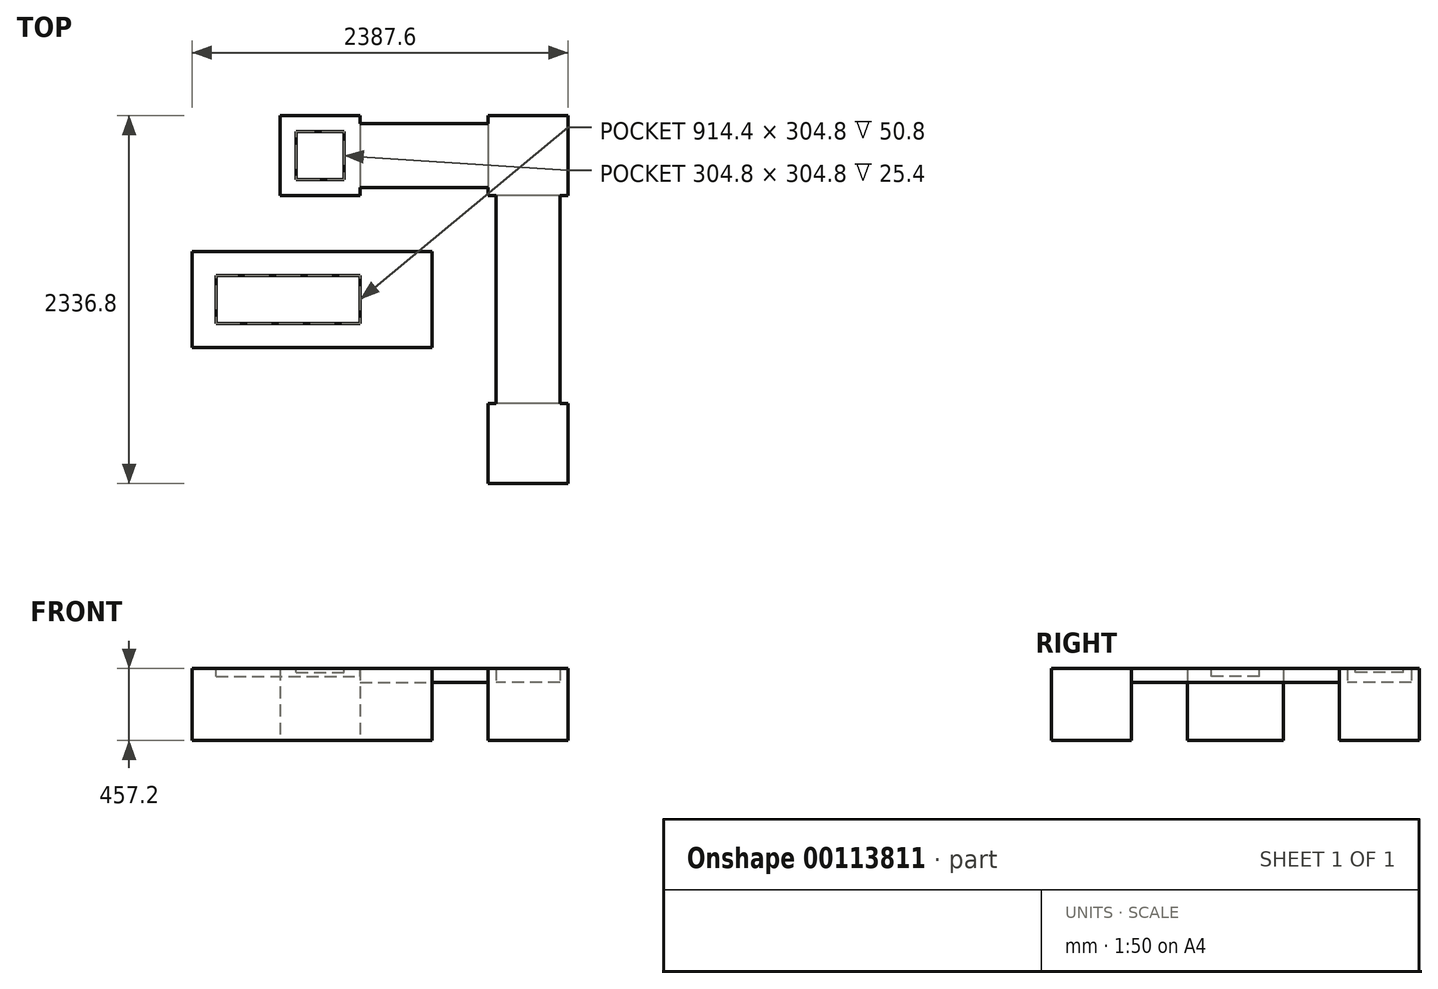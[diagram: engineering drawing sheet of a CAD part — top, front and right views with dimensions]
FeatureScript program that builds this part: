
annotation { "Feature Type Name" : "Feature", "Feature Type Description" : "" }
export const myFeature = defineFeature(function(context is Context, id is Id, definition is map)
    precondition{}
    {
        {
            var Q0;
            Q0=qCreatedBy(makeId("Top.planeOp"),FACE);
            var sketch = newSketch(context, id + "F0", { "sketchPlane" : qUnion([Q0])});
            skLineSegment(sketch, "E0.bottom", {"start": v(-2438.4, 2336.8) * mm, "end": v(0, 2336.8) * mm, "construction": true});
            skLineSegment(sketch, "E0.top", {"start": v(-2438.4, 0) * mm, "end": v(0, 0) * mm, "construction": true});
            skLineSegment(sketch, "E0.left", {"start": v(-2438.4, 2336.8) * mm, "end": v(-2438.4, 0) * mm, "construction": true});
            skLineSegment(sketch, "E0.right", {"start": v(0, 2336.8) * mm, "end": v(0, 0) * mm, "construction": true});
            skLineSegment(sketch, "E1.bottom", {"start": v(0, 2336.8) * mm, "end": v(-508, 2336.8) * mm});
            skLineSegment(sketch, "E1.top", {"start": v(0, 1828.8) * mm, "end": v(-508, 1828.8) * mm});
            skLineSegment(sketch, "E1.left", {"start": v(0, 2336.8) * mm, "end": v(0, 1828.8) * mm});
            skLineSegment(sketch, "E1.right", {"start": v(-508, 2336.8) * mm, "end": v(-508, 1828.8) * mm});
            skLineSegment(sketch, "E2.bottom", {"start": v(0, 0) * mm, "end": v(-508, 0) * mm});
            skLineSegment(sketch, "E2.top", {"start": v(0, 508) * mm, "end": v(-508, 508) * mm});
            skLineSegment(sketch, "E2.left", {"start": v(0, 0) * mm, "end": v(0, 508) * mm});
            skLineSegment(sketch, "E2.right", {"start": v(-508, 0) * mm, "end": v(-508, 508) * mm});
            skLineSegment(sketch, "E3.bottom", {"start": v(-2438.4, 0) * mm, "end": v(-1930.4, 0) * mm});
            skLineSegment(sketch, "E3.top", {"start": v(-2438.4, 508) * mm, "end": v(-1930.4, 508) * mm});
            skLineSegment(sketch, "E3.left", {"start": v(-2438.4, 0) * mm, "end": v(-2438.4, 508) * mm});
            skLineSegment(sketch, "E3.right", {"start": v(-1930.4, 0) * mm, "end": v(-1930.4, 508) * mm});
            skLineSegment(sketch, "E4.bottom", {"start": v(-1828.8, 2336.8) * mm, "end": v(-1320.8, 2336.8) * mm});
            skLineSegment(sketch, "E4.top", {"start": v(-1828.8, 1828.8) * mm, "end": v(-1320.8, 1828.8) * mm});
            skLineSegment(sketch, "E4.left", {"start": v(-1828.8, 2336.8) * mm, "end": v(-1828.8, 1828.8) * mm});
            skLineSegment(sketch, "E4.right", {"start": v(-1320.8, 2336.8) * mm, "end": v(-1320.8, 1828.8) * mm});
            skLineSegment(sketch, "E5.bottom", {"start": v(-2387.6, 1473.2) * mm, "end": v(-863.6, 1473.2) * mm});
            skLineSegment(sketch, "E5.top", {"start": v(-2387.6, 863.6) * mm, "end": v(-863.6, 863.6) * mm});
            skLineSegment(sketch, "E5.left", {"start": v(-2387.6, 1473.2) * mm, "end": v(-2387.6, 863.6) * mm});
            skLineSegment(sketch, "E5.right", {"start": v(-863.6, 1473.2) * mm, "end": v(-863.6, 863.6) * mm});
            skSolve(sketch);
        }
        {
            var Q0;
            Q0=makeQuery(id+"F0.imprint","IMPRINT",FACE,{"disambiguationData":[TD([[makeQuery(id+"F0.imprint","IMPRINT",EDGE,{"derivedFrom":sQuery(id+"F0.wireOp",EDGE,"E2.bottom")}),-1.0]])]});
            var Q1;
            Q1=makeQuery(id+"F0.imprint","IMPRINT",FACE,{"disambiguationData":[TD([[makeQuery(id+"F0.imprint","IMPRINT",EDGE,{"derivedFrom":sQuery(id+"F0.wireOp",EDGE,"E1.bottom")}),1.0]])]});
            var Q2;
            Q2=makeQuery(id+"F0.imprint","IMPRINT",FACE,{"disambiguationData":[TD([[makeQuery(id+"F0.imprint","IMPRINT",EDGE,{"derivedFrom":sQuery(id+"F0.wireOp",EDGE,"E4.bottom")}),-1.0]])]});
            var Q3;
            Q3=makeQuery(id+"F0.imprint","IMPRINT",FACE,{"disambiguationData":[TD([[makeQuery(id+"F0.imprint","IMPRINT",EDGE,{"derivedFrom":sQuery(id+"F0.wireOp",EDGE,"E5.bottom")}),-1.0]])]});
            extrude(context, id + "F1", {"entities" : qUnion([Q0, Q1, Q2, Q3]), "depth" : 457.2 * mm});
        }
        {
            var Q0;
            Q0=makeQuery(id+"F1.opExtrude","CAP_FACE",FACE,{"disambiguationData":[OSD([sQuery(id+"F0.wireOp",EDGE,"E2.bottom"),sQuery(id+"F0.wireOp",EDGE,"E2.top"),sQuery(id+"F0.wireOp",EDGE,"E2.left"),sQuery(id+"F0.wireOp",EDGE,"E2.right")])],"isStart":false});
            var sketch = newSketch(context, id + "F2", { "sketchPlane" : qUnion([Q0])});
            skLineSegment(sketch, "E6.bottom", {"start": v(-457.2, 1879.6) * mm, "end": v(-50.8, 1879.6) * mm});
            skLineSegment(sketch, "E6.top", {"start": v(-457.2, 457.2) * mm, "end": v(-50.8, 457.2) * mm});
            skLineSegment(sketch, "E6.left", {"start": v(-457.2, 1879.6) * mm, "end": v(-457.2, 457.2) * mm});
            skLineSegment(sketch, "E6.right", {"start": v(-50.8, 1879.6) * mm, "end": v(-50.8, 457.2) * mm});
            skPoint(sketch, "E7.0", {"position": v(0, 1828.8) * mm});
            skPoint(sketch, "E8.0", {"position": v(-508, 1828.8) * mm});
            skLineSegment(sketch, "E9.bottom", {"start": v(-1371.6, 2286) * mm, "end": v(-457.2, 2286) * mm});
            skLineSegment(sketch, "E9.top", {"start": v(-1371.6, 1879.6) * mm, "end": v(-457.2, 1879.6) * mm});
            skLineSegment(sketch, "E9.left", {"start": v(-1371.6, 2286) * mm, "end": v(-1371.6, 1879.6) * mm});
            skLineSegment(sketch, "E9.right", {"start": v(-457.2, 2286) * mm, "end": v(-457.2, 1879.6) * mm});
            skLineSegment(sketch, "E10.bottom", {"start": v(-457.2, 457.2) * mm, "end": v(-1981.2, 457.2) * mm});
            skLineSegment(sketch, "E10.top", {"start": v(-457.2, 50.8) * mm, "end": v(-1981.2, 50.8) * mm});
            skLineSegment(sketch, "E10.left", {"start": v(-457.2, 457.2) * mm, "end": v(-457.2, 50.8) * mm});
            skLineSegment(sketch, "E10.right", {"start": v(-1981.2, 457.2) * mm, "end": v(-1981.2, 50.8) * mm});
            skLineSegment(sketch, "E11.bottom", {"start": v(-1727.2, 2235.2) * mm, "end": v(-1422.4, 2235.2) * mm});
            skLineSegment(sketch, "E11.top", {"start": v(-1727.2, 1930.4) * mm, "end": v(-1422.4, 1930.4) * mm});
            skLineSegment(sketch, "E11.left", {"start": v(-1727.2, 2235.2) * mm, "end": v(-1727.2, 1930.4) * mm});
            skLineSegment(sketch, "E11.right", {"start": v(-1422.4, 2235.2) * mm, "end": v(-1422.4, 1930.4) * mm});
            skLineSegment(sketch, "E12.bottom", {"start": v(-2235.2, 1320.8) * mm, "end": v(-1320.8, 1320.8) * mm});
            skLineSegment(sketch, "E12.top", {"start": v(-2235.2, 1016) * mm, "end": v(-1320.8, 1016) * mm});
            skLineSegment(sketch, "E12.left", {"start": v(-2235.2, 1320.8) * mm, "end": v(-2235.2, 1016) * mm});
            skLineSegment(sketch, "E12.right", {"start": v(-1320.8, 1320.8) * mm, "end": v(-1320.8, 1016) * mm});
            skLineSegment(sketch, "E13.0", {"start": v(-2387.6, 1473.2) * mm, "end": v(-2387.6, 863.6) * mm});
            skSolve(sketch);
        }
        {
            var Q0;
            {var subQ0=sQuery(id+"F2.wireOp",EDGE,"E6.bottom");Q0=makeQuery(id+"F2.imprint","IMPRINT",FACE,{"disambiguationData":[TD([[makeQuery(id+"F2.imprint","IMPRINT",EDGE,{"derivedFrom":subQ0}),-1.0]])]});}
            var Q1;
            Q1=makeQuery(id+"F2.imprint","IMPRINT",FACE,{"disambiguationData":[TD([[makeQuery(id+"F2.imprint","IMPRINT",EDGE,{"derivedFrom":sQuery(id+"F2.wireOp",EDGE,"E9.bottom")}),-1.0]])]});
            extrude(context, id + "F3", {"entities" : qUnion([Q0, Q1]), "operationType" : NewBodyOperationType.ADD, "oppositeDirection" : true, "depth" : 88.9 * mm});
        }
        {
            var Q0;
            Q0=makeQuery(id+"F2.imprint","IMPRINT",FACE,{"disambiguationData":[TD([[makeQuery(id+"F2.imprint","IMPRINT",EDGE,{"derivedFrom":sQuery(id+"F2.wireOp",EDGE,"E11.bottom")}),-1.0]])]});
            extrude(context, id + "F4", {"entities" : qUnion([Q0]), "operationType" : NewBodyOperationType.REMOVE, "oppositeDirection" : true, "depth" : 25.4 * mm});
        }
        {
            var Q0;
            Q0=makeQuery(id+"F2.imprint","IMPRINT",FACE,{"disambiguationData":[TD([[makeQuery(id+"F2.imprint","IMPRINT",EDGE,{"derivedFrom":sQuery(id+"F2.wireOp",EDGE,"E12.bottom")}),-1.0]])]});
            extrude(context, id + "F5", {"entities" : qUnion([Q0]), "operationType" : NewBodyOperationType.REMOVE, "oppositeDirection" : true, "depth" : 50.8 * mm});
        }
    });
